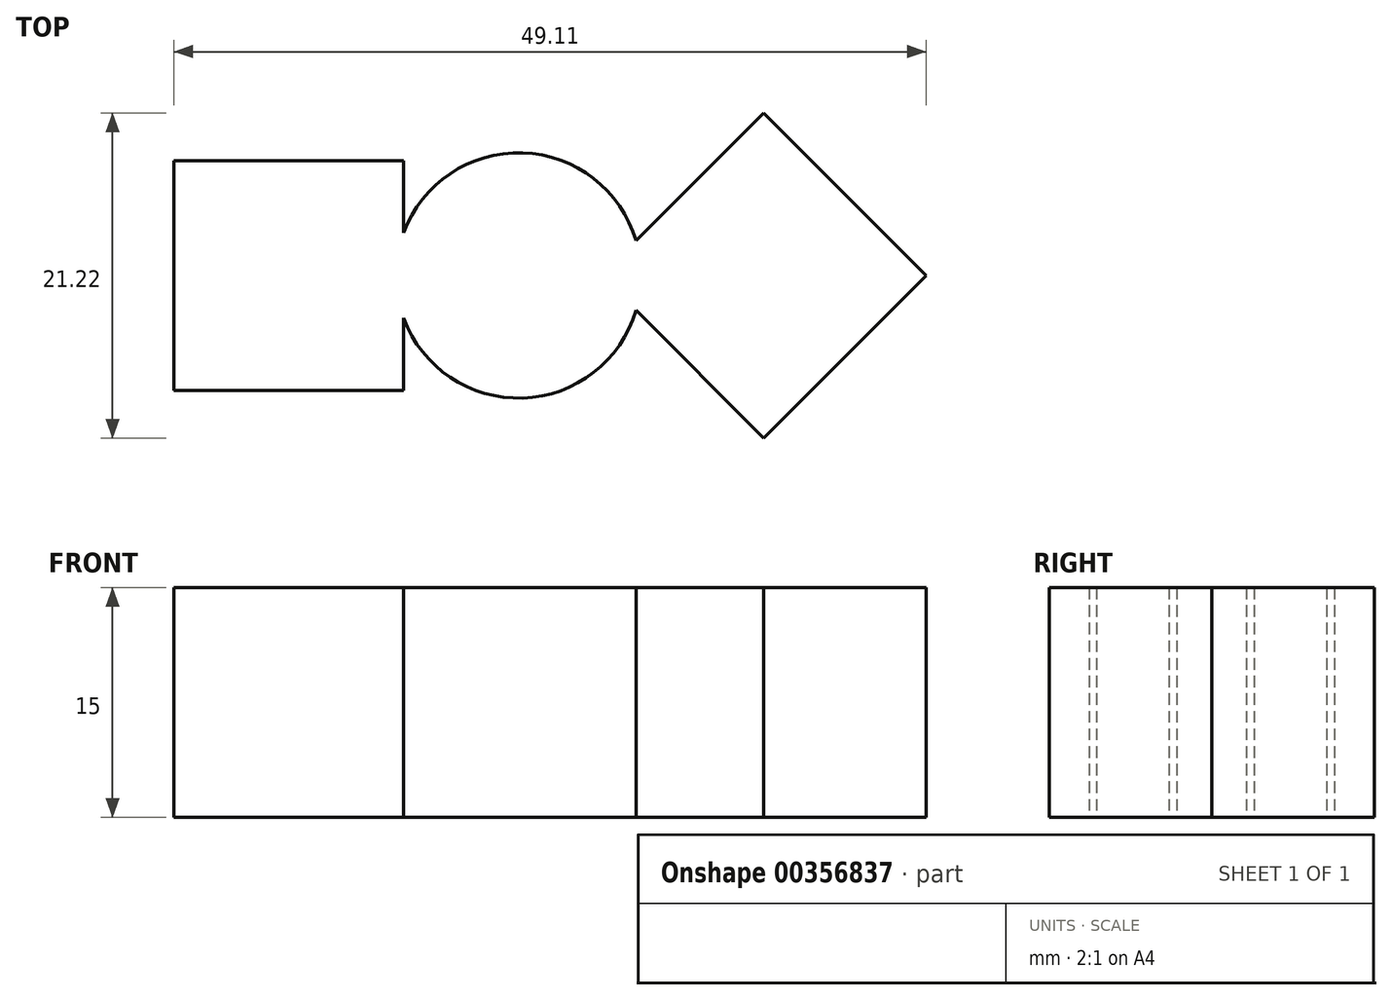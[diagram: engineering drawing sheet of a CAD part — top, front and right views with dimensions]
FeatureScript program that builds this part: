
annotation { "Feature Type Name" : "Feature", "Feature Type Description" : "" }
export const myFeature = defineFeature(function(context is Context, id is Id, definition is map)
    precondition{}
    {
        {
            var Q0;
            Q0=qCreatedBy(makeId("Top.planeOp"), FACE);
            var sketch = newSketch(context, id + "F0", { "sketchPlane" : qUnion([Q0])});
            skLineSegment(sketch, "E0.bottom", {"start": v(-15, 0) * mm, "end": v(0, 0) * mm});
            skLineSegment(sketch, "E0.top", {"start": v(-15, 15) * mm, "end": v(0, 15) * mm});
            skLineSegment(sketch, "E0.left", {"start": v(-15, 0) * mm, "end": v(-15, 15) * mm});
            skLineSegment(sketch, "E0.right", {"start": v(0, 0) * mm, "end": v(0, 15) * mm});
            skLineSegment(sketch, "E1", {"start": v(0, 7.5) * mm, "end": v(55.13, 7.5) * mm, "construction": true});
            skCircle(sketch, "E2", {"center": v(7.5, 7.5) * mm, "radius": 8 * mm});
            skLineSegment(sketch, "E3.bottom", {"start": v(34.1, 7.5) * mm, "end": v(23.5, 18.1) * mm});
            skLineSegment(sketch, "E3.top", {"start": v(23.5, -3.1) * mm, "end": v(12.9, 7.5) * mm});
            skLineSegment(sketch, "E3.left", {"start": v(34.1, 7.5) * mm, "end": v(23.5, -3.1) * mm});
            skLineSegment(sketch, "E3.right", {"start": v(23.5, 18.1) * mm, "end": v(12.9, 7.5) * mm});
            skPoint(sketch, "E3.middle", {"position": v(23.5, 7.5) * mm});
            skSolve(sketch);
        }
        {
            var Q0;
            Q0 = qSketchRegion(id + "F0", true);
            extrude(context, id + "F1", {"entities" : qUnion([Q0]), "depth" : 15 * mm, "offsetDistance" : 25 * mm});
        }
    });
